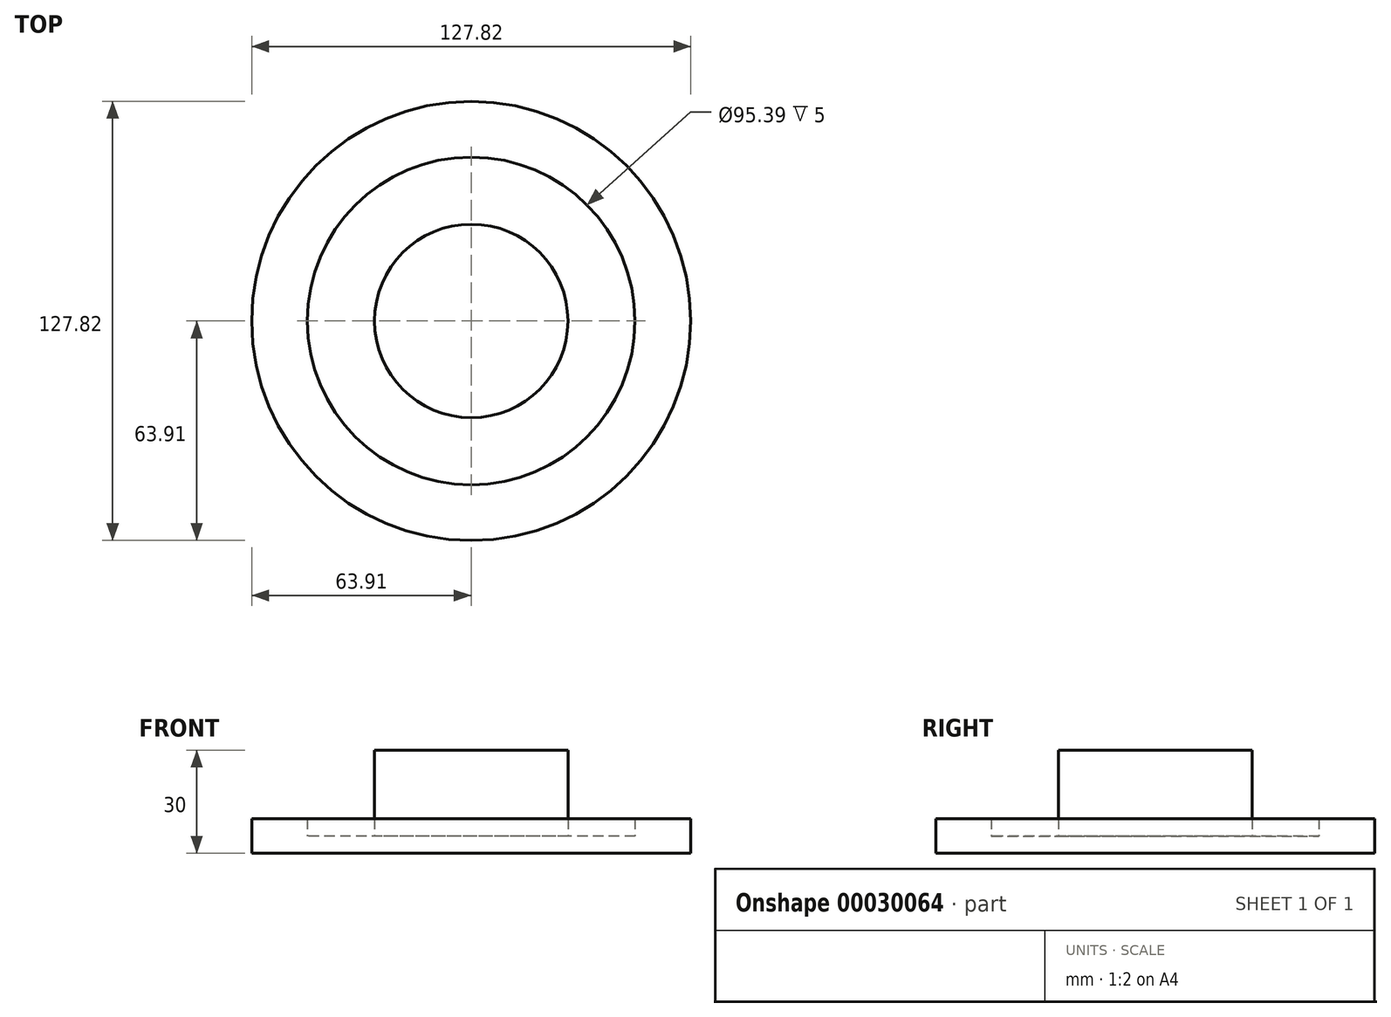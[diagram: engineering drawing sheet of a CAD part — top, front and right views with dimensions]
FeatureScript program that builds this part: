
annotation { "Feature Type Name" : "Feature", "Feature Type Description" : "" }
export const myFeature = defineFeature(function(context is Context, id is Id, definition is map)
    precondition{}
    {
        {
            var Q0;
            Q0=qCreatedBy(makeId("Top.planeOp"),FACE);
            var sketch = newSketch(context, id + "F0", { "sketchPlane" : qUnion([Q0])});
            skCircle(sketch, "E0", {"center": v(0, 0) * mm, "radius": 28.16 * mm});
            skCircle(sketch, "E1", {"center": v(0, 0) * mm, "radius": 47.7 * mm});
            skCircle(sketch, "E2", {"center": v(0, 0) * mm, "radius": 63.9 * mm});
            skSolve(sketch);
        }
        {
            var Q0;
            Q0=makeQuery(id+"F0.imprint","IMPRINT",FACE,{"disambiguationData":[TD([[makeQuery(id+"F0.imprint","IMPRINT",EDGE,{"derivedFrom":sQuery(id+"F0.wireOp",EDGE,"E0")}),1.0]])]});
            extrude(context, id + "F1", {"entities" : qUnion([Q0]), "depth" : 30 * mm});
        }
        {
            var Q0;
            Q0=makeQuery(id+"F0.imprint","IMPRINT",FACE,{"disambiguationData":[TD([[makeQuery(id+"F0.imprint","IMPRINT",EDGE,{"derivedFrom":sQuery(id+"F0.wireOp",EDGE,"E0")}),-1.0]])]});
            extrude(context, id + "F2", {"entities" : qUnion([Q0]), "operationType" : NewBodyOperationType.ADD, "depth" : 5 * mm});
        }
        {
            var Q0;
            Q0=makeQuery(id+"F0.imprint","IMPRINT",FACE,{"disambiguationData":[TD([[makeQuery(id+"F0.imprint","IMPRINT",EDGE,{"derivedFrom":sQuery(id+"F0.wireOp",EDGE,"E1")}),-1.0]])]});
            extrude(context, id + "F3", {"entities" : qUnion([Q0]), "operationType" : NewBodyOperationType.ADD, "depth" : 10 * mm});
        }
    });
